# Revit family: Indoor_Table Lamp_Santa&Cole_Sin S-L
name_source: partatom
category: Luminarias
revit_build: Autodesk Revit 2018 (Build: 20190510_1515(x64)
units: mm (PartAtom-declared; Revit-internal decimal feet)

## family parameters
Compartido = No
Corte con vacíos al cargar = No
Cota de conector redondo = Diámetro de uso
Número OmniClass = 23.80.70.00
Origen de luz = Sí
Punto de cálculo de habitación = No
Se basa en plano de trabajo = No
Siempre vertical = Sí
Tipo de pieza = Normal
Título OmniClass = Lighting

## types (10) — shared parameters
Assembly instructions - CE = https://www.santacole.com
Assembly instructions - UL = https://www.santacole.com
Cambio de temperatura de color de luz atenuada = <Ninguno>
Energy Label = https://www.santacole.com
Fabricante = Santa & Cole
Filtro de color = 16777215
Forma visible en renderización = No
Manufacturer website = http://www.santacole.com
Modelo = Sin
Technical Information = https://www.santacole.com
URL = https://www.santacole.com
Ángulo de inclinación = 90.00°

## per-type parameters (varying)
| type | Archivo de red fotométrica | Carga aparente | Code | Diámetro de círculo de emisión | Lampshade Material | Light Source Elevation | Load | Structure Material | Visibility_Lampshade_Sin L | Visibility_Lampshade_Sin S | Visibility_Sin L | Visibility_Sin S |
| Sin L - S&C White Metal Structure with Methacrylate Lampshade | SIN3x+SINL1.IES | 25 VA | SIN2x | 50 mm | Santa & Cole - White Methacrylate | 560 mm | 25 W | Santa & Cole - White Matte Finish | Sí | No | Sí | No |
| Sin L - S&C White Metal Structure with Aluminium Lampshade | SIN3x+SINL1.IES | 25 VA | SIN3x+SINLx | 50 mm | Santa & Cole - Aluminium | 560 mm | 25 W | Santa & Cole - White Matte Finish | Sí | No | Sí | No |
| Sin L - S&C White Metal Structure | SIN3x.IES | 25 VA | SIN3x | 50 mm | Santa & Cole - Aluminium | 560 mm | 25 W | Santa & Cole - White Matte Finish | No | No | Sí | No |
| Sin L - Graphite Metal Structure | SIN3x.IES | 25 VA | SIN3x | 50 mm | Santa & Cole - Aluminium | 560 mm | 25 W | Santa & Cole - Metallic Graphite Grey | No | No | Sí | No |
| Sin L - Graphite Metal Structure with Aluminium Lampshade | SIN3x+SINL1.IES | 25 VA | SIN3x+SINLx | 50 mm | Santa & Cole - Aluminium | 560 mm | 25 W | Santa & Cole - Metallic Graphite Grey | Sí | No | Sí | No |
| Sin S - Graphite Metal Structure | SIN2x.IES | 13 VA | SIN2x | 50 mm | Santa & Cole - Aluminium | 360 mm | 13 W | Santa & Cole - Metallic Graphite Grey | No | No | No | Sí |
| Sin S - Graphite Metal Structure with Aluminium Lampshade | SIN2x+SINS1.IES | 13 VA | SIN2x+SINSx | 50 mm | Santa & Cole - Aluminium | 360 mm | 13 W | Santa & Cole - Metallic Graphite Grey | No | Sí | No | Sí |
| Sin S - S&C White Metal Structure | SIN2x.IES | 13 VA | SIN2x | 50 mm | Santa & Cole - Aluminium | 360 mm | 13 W | Santa & Cole - White Matte Finish | No | No | No | Sí |
| Sin S - S&C White Metal Structure with Aluminium Lampshade | SIN2x+SINS1.IES | 13 VA | SIN2x+SINSx | 50 mm | Santa & Cole - Aluminium | 360 mm | 13 W | Santa & Cole - White Matte Finish | No | Sí | No | Sí |
| Sin S - S&C White Metal Structure with Methacrylate Lampshade | SIN2x+SINS1.IES | 13 VA | SIN2x+SINSx | 250 mm  [stored 0.82021 ft] | Santa & Cole - White Methacrylate | 340 mm  [stored 1.11549 ft] | 13 W | Santa & Cole - White Matte Finish | No | Sí | No | Sí |

note: [stored X ft] marks values corroborated as IEEE doubles in the binary element streams (Revit-internal decimal feet)

## geometry (parser evidence)
native form markers: Sweep x3
no freeform markers — native parametric forms only
